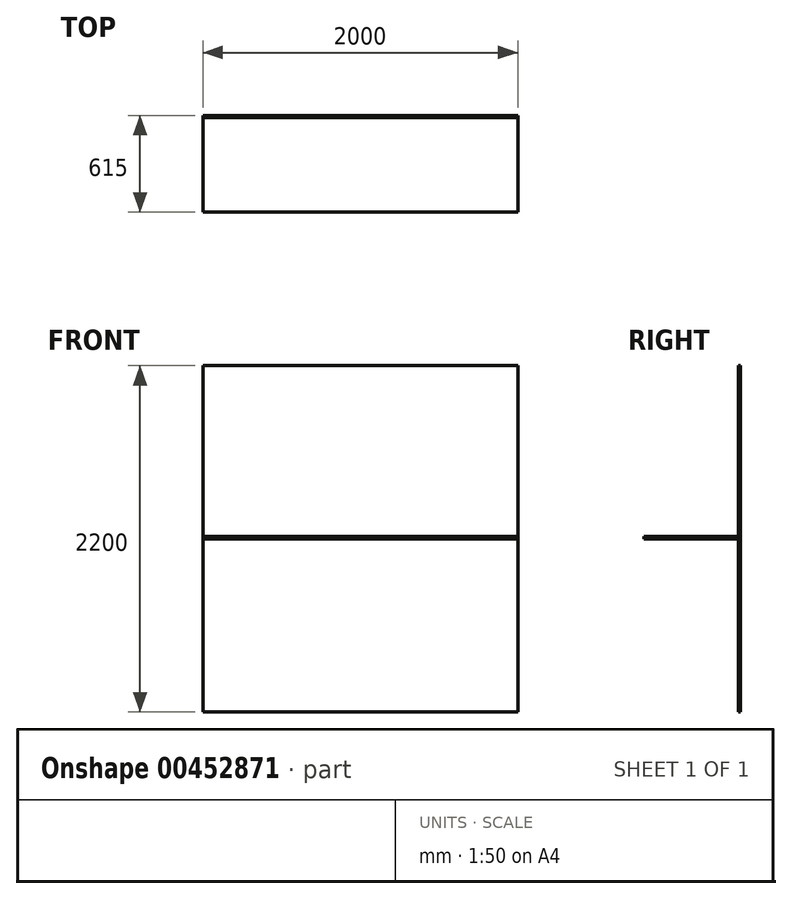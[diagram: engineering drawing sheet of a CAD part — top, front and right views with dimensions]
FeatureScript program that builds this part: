
annotation { "Feature Type Name" : "Feature", "Feature Type Description" : "" }
export const myFeature = defineFeature(function(context is Context, id is Id, definition is map)
    precondition{}
    {
        {
            var Q0;
            Q0=qCreatedBy(makeId("Front.planeOp"),FACE);
            var sketch = newSketch(context, id + "F0", { "sketchPlane" : qUnion([Q0])});
            skLineSegment(sketch, "E0.bottom", {"start": v(-1000, -1100) * mm, "end": v(1000, -1100) * mm});
            skLineSegment(sketch, "E0.top", {"start": v(-1000, 1100) * mm, "end": v(1000, 1100) * mm});
            skLineSegment(sketch, "E0.left", {"start": v(-1000, -1100) * mm, "end": v(-1000, 1100) * mm});
            skLineSegment(sketch, "E0.right", {"start": v(1000, -1100) * mm, "end": v(1000, 1100) * mm});
            skPoint(sketch, "E0.middle", {"position": v(0, 0) * mm});
            skSolve(sketch);
        }
        {
            var Q0;
            Q0=makeQuery(id+"F0.imprint","IMPRINT",FACE,{"disambiguationData":[TD([[makeQuery(id+"F0.imprint","IMPRINT",EDGE,{"derivedFrom":sQuery(id+"F0.wireOp",EDGE,"E0.bottom")}),1.0]])]});
            extrude(context, id + "F1", {"entities" : qUnion([Q0]), "depth" : 15 * mm});
        }
        {
            var Q0;
            Q0=qCreatedBy(makeId("Top.planeOp"),FACE);
            var sketch = newSketch(context, id + "F2", { "sketchPlane" : qUnion([Q0])});
            skLineSegment(sketch, "E1.bottom", {"start": v(-1000, -15) * mm, "end": v(1000, -15) * mm});
            skLineSegment(sketch, "E1.top", {"start": v(-1000, -615) * mm, "end": v(1000, -615) * mm});
            skLineSegment(sketch, "E1.left", {"start": v(-1000, -15) * mm, "end": v(-1000, -615) * mm});
            skLineSegment(sketch, "E1.right", {"start": v(1000, -15) * mm, "end": v(1000, -615) * mm});
            skSolve(sketch);
        }
        {
            var Q0;
            Q0=makeQuery(id+"F2.imprint","IMPRINT",FACE,{"disambiguationData":[TD([[makeQuery(id+"F2.imprint","IMPRINT",EDGE,{"derivedFrom":sQuery(id+"F2.wireOp",EDGE,"E1.bottom")}),-1.0]])]});
            extrude(context, id + "F3", {"entities" : qUnion([Q0]), "depth" : 15 * mm});
        }
    });
